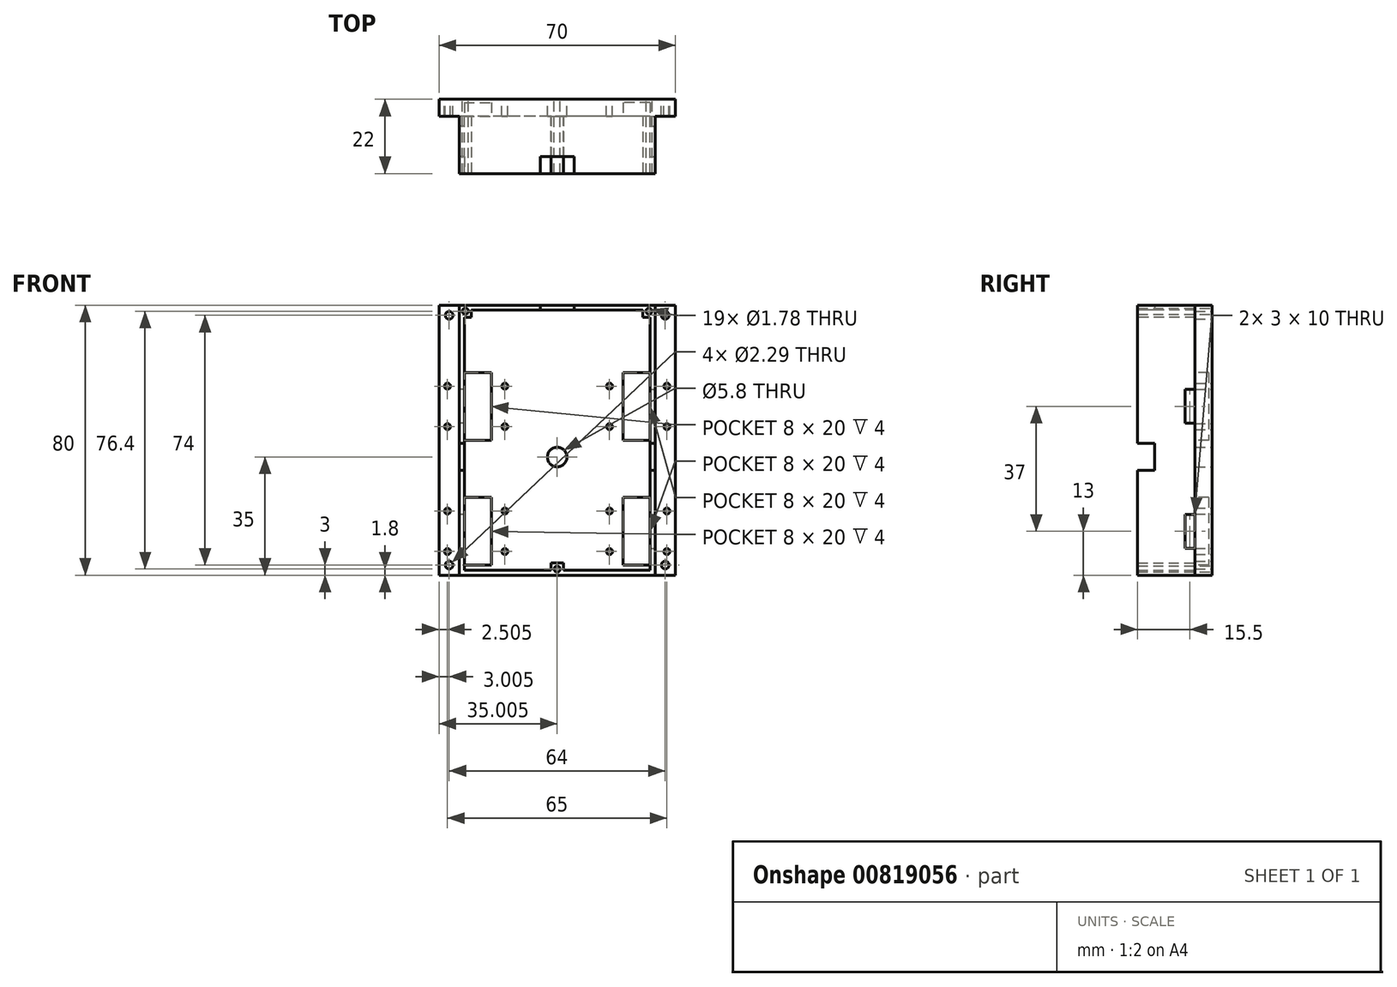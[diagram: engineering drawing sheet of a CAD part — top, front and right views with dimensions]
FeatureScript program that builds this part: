
annotation { "Feature Type Name" : "Feature", "Feature Type Description" : "" }
export const myFeature = defineFeature(function(context is Context, id is Id, definition is map)
    precondition{}
    {
        {
            var Q0;
            Q0=qCreatedBy(makeId("Front.planeOp"),FACE);
            var sketch = newSketch(context, id + "F0", { "sketchPlane" : qUnion([Q0])});
            skCircle(sketch, "E0", {"center": v(-20.58, 45.7) * mm, "radius": 0.89 * mm});
            skCircle(sketch, "E1", {"center": v(-25.88, 23.5) * mm, "radius": 0.89 * mm});
            skCircle(sketch, "E2", {"center": v(-8.88, 23.5) * mm, "radius": 0.89 * mm});
            skCircle(sketch, "E3", {"center": v(-8.88, 11.5) * mm, "radius": 0.89 * mm});
            skCircle(sketch, "E4", {"center": v(-25.88, 11.5) * mm, "radius": 0.89 * mm});
            skCircle(sketch, "E5", {"center": v(-25.88, -13.5) * mm, "radius": 0.89 * mm});
            skCircle(sketch, "E6", {"center": v(-8.88, -13.5) * mm, "radius": 0.89 * mm});
            skCircle(sketch, "E7", {"center": v(-8.88, -25.5) * mm, "radius": 0.89 * mm});
            skCircle(sketch, "E8", {"center": v(-25.88, -25.5) * mm, "radius": 0.89 * mm});
            skCircle(sketch, "E9", {"center": v(-25.38, -29.5) * mm, "radius": 1.14 * mm});
            skCircle(sketch, "E10", {"center": v(6.62, -30.7) * mm, "radius": 0.89 * mm});
            skCircle(sketch, "E11", {"center": v(6.62, 2.5) * mm, "radius": 2.9 * mm});
            skLineSegment(sketch, "E12", {"start": v(41.63, 47.5) * mm, "end": v(-28.38, 47.5) * mm});
            skLineSegment(sketch, "E13", {"start": v(-28.37, 47.5) * mm, "end": v(-28.38, -32.5) * mm});
            skLineSegment(sketch, "E14", {"start": v(41.63, -32.5) * mm, "end": v(-28.38, -32.5) * mm});
            skLineSegment(sketch, "E15.bottom", {"start": v(-28.38, -32.5) * mm, "end": v(-22.38, -32.5) * mm, "construction": true});
            skLineSegment(sketch, "E15.top", {"start": v(-28.38, -26.5) * mm, "end": v(-22.38, -26.5) * mm, "construction": true});
            skLineSegment(sketch, "E15.left", {"start": v(-28.38, -32.5) * mm, "end": v(-28.38, -26.5) * mm, "construction": true});
            skLineSegment(sketch, "E15.right", {"start": v(-22.38, -32.5) * mm, "end": v(-22.38, -26.5) * mm, "construction": true});
            skLineSegment(sketch, "E16", {"start": v(-28.37, -26.5) * mm, "end": v(-22.38, -32.5) * mm});
            skLineSegment(sketch, "E17", {"start": v(-28.38, -32.5) * mm, "end": v(-22.38, -26.5) * mm});
            skPoint(sketch, "E18", {"position": v(-28.38, 7.5) * mm});
            skLineSegment(sketch, "E19", {"start": v(6.62, 47.5) * mm, "end": v(-20.58, 47.5) * mm, "construction": true});
            skLineSegment(sketch, "E20", {"start": v(-20.58, 47.5) * mm, "end": v(-20.58, 45.7) * mm});
            skLineSegment(sketch, "E21", {"start": v(6.63, -32.5) * mm, "end": v(6.63, -30.7) * mm});
            skLineSegment(sketch, "E22", {"start": v(-8.88, -13.5) * mm, "end": v(-8.88, -25.5) * mm, "construction": true});
            skPoint(sketch, "E23", {"position": v(-8.88, -19.5) * mm});
            skLineSegment(sketch, "E24", {"start": v(-8.88, -19.5) * mm, "end": v(-28.38, -19.5) * mm, "construction": true});
            skLineSegment(sketch, "E25", {"start": v(-25.88, -25.5) * mm, "end": v(-25.88, -13.5) * mm, "construction": true});
            skPoint(sketch, "E26", {"position": v(-25.88, -19.5) * mm});
            skPoint(sketch, "E27", {"position": v(-20.88, -19.5) * mm});
            skLineSegment(sketch, "E28", {"start": v(-20.88, -19.5) * mm, "end": v(-20.88, -9.5) * mm, "construction": true});
            skLineSegment(sketch, "E29", {"start": v(-20.88, -9.5) * mm, "end": v(-12.88, -9.5) * mm, "construction": true});
            skLineSegment(sketch, "E30", {"start": v(-12.88, -9.5) * mm, "end": v(-12.88, -29.5) * mm, "construction": true});
            skLineSegment(sketch, "E31.bottom", {"start": v(-20.88, -9.5) * mm, "end": v(-12.88, -9.5) * mm});
            skLineSegment(sketch, "E31.top", {"start": v(-20.88, -29.5) * mm, "end": v(-12.88, -29.5) * mm});
            skLineSegment(sketch, "E31.left", {"start": v(-20.88, -9.5) * mm, "end": v(-20.88, -29.5) * mm});
            skLineSegment(sketch, "E31.right", {"start": v(-12.88, -9.5) * mm, "end": v(-12.88, -29.5) * mm});
            skLineSegment(sketch, "E32", {"start": v(-25.88, 23.5) * mm, "end": v(-25.88, 11.5) * mm, "construction": true});
            skPoint(sketch, "E33", {"position": v(-25.88, 17.5) * mm});
            skLineSegment(sketch, "E34", {"start": v(-8.88, 23.5) * mm, "end": v(-8.88, 11.5) * mm, "construction": true});
            skPoint(sketch, "E35", {"position": v(-8.88, 17.5) * mm});
            skLineSegment(sketch, "E36", {"start": v(-8.88, 17.5) * mm, "end": v(-28.38, 17.5) * mm, "construction": true});
            skLineSegment(sketch, "E37", {"start": v(-25.88, 23.5) * mm, "end": v(-28.38, 23.5) * mm, "construction": true});
            skLineSegment(sketch, "E38", {"start": v(-25.88, -13.5) * mm, "end": v(-28.38, -13.5) * mm, "construction": true});
            skLineSegment(sketch, "E39", {"start": v(-20.88, -9.5) * mm, "end": v(-28.38, -9.5) * mm, "construction": true});
            skLineSegment(sketch, "E40", {"start": v(-28.38, 27.5) * mm, "end": v(-20.88, 27.5) * mm, "construction": true});
            skLineSegment(sketch, "E41", {"start": v(-20.88, 27.5) * mm, "end": v(-20.88, 17.5) * mm});
            skLineSegment(sketch, "E42", {"start": v(-20.88, 27.5) * mm, "end": v(-12.88, 27.5) * mm});
            skLineSegment(sketch, "E43", {"start": v(-12.88, 27.5) * mm, "end": v(-12.87, 7.5) * mm, "construction": true});
            skLineSegment(sketch, "E44.bottom", {"start": v(-20.88, 27.5) * mm, "end": v(-12.88, 27.5) * mm, "construction": true});
            skLineSegment(sketch, "E44.top", {"start": v(-20.88, 7.5) * mm, "end": v(-12.88, 7.5) * mm});
            skLineSegment(sketch, "E44.left", {"start": v(-20.88, 27.5) * mm, "end": v(-20.88, 7.5) * mm});
            skLineSegment(sketch, "E44.right", {"start": v(-12.87, 27.5) * mm, "end": v(-12.87, 7.5) * mm});
            skLineSegment(sketch, "E45", {"start": v(41.62, 47.5) * mm, "end": v(41.63, -32.5) * mm});
            skLineSegment(sketch, "E46", {"start": v(6.62, 2.5) * mm, "end": v(6.62, -30.7) * mm});
            skLineSegment(sketch, "E47", {"start": v(6.62, 47.5) * mm, "end": v(6.62, 2.5) * mm, "construction": true});
            skLineSegment(sketch, "E48.bottom", {"start": v(-28.38, 47.5) * mm, "end": v(-22.38, 47.5) * mm, "construction": true});
            skLineSegment(sketch, "E48.top", {"start": v(-28.38, 41.5) * mm, "end": v(-22.38, 41.5) * mm, "construction": true});
            skLineSegment(sketch, "E48.left", {"start": v(-28.38, 47.5) * mm, "end": v(-28.38, 41.5) * mm, "construction": true});
            skLineSegment(sketch, "E48.right", {"start": v(-22.38, 47.5) * mm, "end": v(-22.38, 41.5) * mm, "construction": true});
            skLineSegment(sketch, "E49", {"start": v(-28.38, 47.5) * mm, "end": v(-22.38, 41.5) * mm, "construction": true});
            skLineSegment(sketch, "E50", {"start": v(-28.38, 41.5) * mm, "end": v(-22.38, 47.5) * mm, "construction": true});
            skCircle(sketch, "E51", {"center": v(-25.38, 44.5) * mm, "radius": 1.14 * mm});
            skCircle(sketch, "E52.MirrorC", {"center": v(38.62, -29.5) * mm, "radius": 1.14 * mm});
            skCircle(sketch, "E53.MirrorC", {"center": v(39.12, -25.5) * mm, "radius": 0.89 * mm});
            skLineSegment(sketch, "E54.MirrorCS", {"start": v(26.13, -9.5) * mm, "end": v(26.13, -29.5) * mm});
            skLineSegment(sketch, "E55.MirrorCS", {"start": v(34.12, -9.5) * mm, "end": v(26.13, -9.5) * mm});
            skLineSegment(sketch, "E56.MirrorCS", {"start": v(34.12, -9.5) * mm, "end": v(34.12, -29.5) * mm});
            skPoint(sketch, "E57.MirrorP", {"position": v(34.12, -19.5) * mm});
            skLineSegment(sketch, "E58.MirrorCS", {"start": v(34.12, -9.5) * mm, "end": v(26.13, -9.5) * mm, "construction": true});
            skLineSegment(sketch, "E59.MirrorCS", {"start": v(22.13, -13.5) * mm, "end": v(22.13, -25.5) * mm, "construction": true});
            skLineSegment(sketch, "E60.MirrorCS", {"start": v(34.12, -29.5) * mm, "end": v(26.13, -29.5) * mm});
            skLineSegment(sketch, "E61.MirrorCS", {"start": v(34.12, -19.5) * mm, "end": v(34.12, -9.5) * mm, "construction": true});
            skCircle(sketch, "E62.MirrorC", {"center": v(22.13, -25.5) * mm, "radius": 0.89 * mm});
            skCircle(sketch, "E63.MirrorC", {"center": v(22.13, -13.5) * mm, "radius": 0.89 * mm});
            skPoint(sketch, "E64.MirrorP", {"position": v(39.12, -19.5) * mm});
            skPoint(sketch, "E65.MirrorP", {"position": v(22.13, -19.5) * mm});
            skCircle(sketch, "E66.MirrorC", {"center": v(39.12, -13.5) * mm, "radius": 0.89 * mm});
            skLineSegment(sketch, "E67.MirrorCS", {"start": v(39.12, -25.5) * mm, "end": v(39.12, -13.5) * mm, "construction": true});
            skLineSegment(sketch, "E68.MirrorCS", {"start": v(26.13, -9.5) * mm, "end": v(26.13, -29.5) * mm, "construction": true});
            skPoint(sketch, "E69.MirrorP", {"position": v(41.63, 7.5) * mm});
            skLineSegment(sketch, "E70.MirrorCS", {"start": v(26.12, 27.5) * mm, "end": v(26.12, 7.5) * mm});
            skLineSegment(sketch, "E71.MirrorCS", {"start": v(34.12, 27.5) * mm, "end": v(26.13, 27.5) * mm});
            skCircle(sketch, "E72.MirrorC", {"center": v(39.13, 23.5) * mm, "radius": 0.89 * mm});
            skLineSegment(sketch, "E73.MirrorCS", {"start": v(34.12, 27.5) * mm, "end": v(26.13, 27.5) * mm, "construction": true});
            skLineSegment(sketch, "E74.MirrorCS", {"start": v(34.12, 7.5) * mm, "end": v(26.12, 7.5) * mm});
            skPoint(sketch, "E75.MirrorP", {"position": v(39.13, 17.5) * mm});
            skLineSegment(sketch, "E76.MirrorCS", {"start": v(34.12, 27.5) * mm, "end": v(34.12, 7.5) * mm});
            skCircle(sketch, "E77.MirrorC", {"center": v(22.13, 23.5) * mm, "radius": 0.89 * mm});
            skLineSegment(sketch, "E78.MirrorCS", {"start": v(22.13, 23.5) * mm, "end": v(22.13, 11.5) * mm, "construction": true});
            skLineSegment(sketch, "E79.MirrorCS", {"start": v(26.12, 27.5) * mm, "end": v(26.12, 7.5) * mm, "construction": true});
            skLineSegment(sketch, "E80.MirrorCS", {"start": v(39.12, 23.5) * mm, "end": v(39.12, 11.5) * mm, "construction": true});
            skLineSegment(sketch, "E81.MirrorCS", {"start": v(34.12, 27.5) * mm, "end": v(34.12, 17.5) * mm});
            skCircle(sketch, "E82.MirrorC", {"center": v(39.13, 11.5) * mm, "radius": 0.89 * mm});
            skCircle(sketch, "E83.MirrorC", {"center": v(22.13, 11.5) * mm, "radius": 0.89 * mm});
            skPoint(sketch, "E84.MirrorP", {"position": v(22.13, 17.5) * mm});
            skCircle(sketch, "E85.MirrorC", {"center": v(38.63, 44.5) * mm, "radius": 1.14 * mm});
            skCircle(sketch, "E86.MirrorC", {"center": v(33.83, 45.7) * mm, "radius": 0.89 * mm});
            skLineSegment(sketch, "E87", {"start": v(34.12, -29.5) * mm, "end": v(35.62, -29.5) * mm, "construction": true});
            skLineSegment(sketch, "E88", {"start": v(35.62, -29.5) * mm, "end": v(35.62, -32.5) * mm});
            skLineSegment(sketch, "E89", {"start": v(35.62, -29.5) * mm, "end": v(35.62, 47.5) * mm});
            skLineSegment(sketch, "E90", {"start": v(-20.88, -29.5) * mm, "end": v(-22.38, -29.5) * mm, "construction": true});
            skLineSegment(sketch, "E91.bottom", {"start": v(-22.38, 47.5) * mm, "end": v(35.62, 47.5) * mm});
            skLineSegment(sketch, "E91.top", {"start": v(-22.38, -32.5) * mm, "end": v(35.62, -32.5) * mm});
            skLineSegment(sketch, "E91.left", {"start": v(-22.38, 47.5) * mm, "end": v(-22.38, -32.5) * mm});
            skLineSegment(sketch, "E91.right", {"start": v(35.62, 47.5) * mm, "end": v(35.62, -32.5) * mm});
            skLineSegment(sketch, "E92", {"start": v(-20.58, 45.7) * mm, "end": v(-18.78, 45.7) * mm, "construction": true});
            skLineSegment(sketch, "E93", {"start": v(-18.78, 45.7) * mm, "end": v(-18.78, 43.9) * mm, "construction": true});
            skLineSegment(sketch, "E94.bottom", {"start": v(-18.78, 43.9) * mm, "end": v(-22.38, 43.9) * mm});
            skLineSegment(sketch, "E94.top", {"start": v(-18.78, 47.5) * mm, "end": v(-22.38, 47.5) * mm});
            skLineSegment(sketch, "E94.left", {"start": v(-18.78, 43.9) * mm, "end": v(-18.78, 47.5) * mm});
            skLineSegment(sketch, "E94.right", {"start": v(-22.38, 43.9) * mm, "end": v(-22.38, 47.5) * mm});
            skLineSegment(sketch, "E95", {"start": v(33.83, 45.7) * mm, "end": v(32.03, 45.7) * mm, "construction": true});
            skLineSegment(sketch, "E96", {"start": v(32.03, 45.7) * mm, "end": v(32.03, 43.9) * mm, "construction": true});
            skLineSegment(sketch, "E97.bottom", {"start": v(32.03, 43.9) * mm, "end": v(35.62, 43.9) * mm});
            skLineSegment(sketch, "E97.top", {"start": v(32.03, 47.5) * mm, "end": v(35.62, 47.5) * mm});
            skLineSegment(sketch, "E97.left", {"start": v(32.03, 43.9) * mm, "end": v(32.03, 47.5) * mm});
            skLineSegment(sketch, "E97.right", {"start": v(35.62, 43.9) * mm, "end": v(35.62, 47.5) * mm});
            skLineSegment(sketch, "E98", {"start": v(6.62, -30.7) * mm, "end": v(4.82, -30.7) * mm});
            skLineSegment(sketch, "E99", {"start": v(4.82, -30.7) * mm, "end": v(4.82, -28.9) * mm});
            skLineSegment(sketch, "E100", {"start": v(6.63, -32.5) * mm, "end": v(8.43, -32.5) * mm});
            skLineSegment(sketch, "E101.bottom", {"start": v(8.43, -32.5) * mm, "end": v(4.82, -32.5) * mm});
            skLineSegment(sketch, "E101.top", {"start": v(8.43, -28.9) * mm, "end": v(4.82, -28.9) * mm});
            skLineSegment(sketch, "E101.left", {"start": v(8.43, -32.5) * mm, "end": v(8.43, -28.9) * mm});
            skLineSegment(sketch, "E101.right", {"start": v(4.82, -32.5) * mm, "end": v(4.82, -28.9) * mm});
            skLineSegment(sketch, "E102", {"start": v(34.13, 17.5) * mm, "end": v(37.13, 17.5) * mm, "construction": true});
            skLineSegment(sketch, "E103.bottom", {"start": v(33.13, 22.5) * mm, "end": v(37.13, 22.5) * mm});
            skLineSegment(sketch, "E103.top", {"start": v(33.13, 12.5) * mm, "end": v(37.13, 12.5) * mm});
            skLineSegment(sketch, "E103.left", {"start": v(33.12, 22.5) * mm, "end": v(33.12, 12.5) * mm});
            skLineSegment(sketch, "E103.right", {"start": v(37.13, 22.5) * mm, "end": v(37.13, 12.5) * mm});
            skPoint(sketch, "E104", {"position": v(37.13, 17.5) * mm});
            skLineSegment(sketch, "E105.MirrorCS", {"start": v(-19.88, 12.5) * mm, "end": v(-23.88, 12.5) * mm});
            skLineSegment(sketch, "E106.MirrorCS", {"start": v(-23.87, 22.5) * mm, "end": v(-23.87, 12.5) * mm});
            skLineSegment(sketch, "E107.MirrorCS", {"start": v(-19.87, 22.5) * mm, "end": v(-19.87, 12.5) * mm});
            skLineSegment(sketch, "E108.MirrorCS", {"start": v(-19.88, 22.5) * mm, "end": v(-23.88, 22.5) * mm});
            skLineSegment(sketch, "E109", {"start": v(34.12, -19.5) * mm, "end": v(37.13, -19.5) * mm, "construction": true});
            skLineSegment(sketch, "E110.bottom", {"start": v(33.12, -14.5) * mm, "end": v(37.13, -14.5) * mm});
            skLineSegment(sketch, "E110.top", {"start": v(33.12, -24.5) * mm, "end": v(37.13, -24.5) * mm});
            skLineSegment(sketch, "E110.left", {"start": v(33.12, -14.5) * mm, "end": v(33.12, -24.5) * mm});
            skLineSegment(sketch, "E110.right", {"start": v(37.13, -14.5) * mm, "end": v(37.13, -24.5) * mm});
            skPoint(sketch, "E111", {"position": v(37.13, -19.5) * mm});
            skLineSegment(sketch, "E112.MirrorCS", {"start": v(-19.88, -24.5) * mm, "end": v(-23.88, -24.5) * mm});
            skLineSegment(sketch, "E113.MirrorCS", {"start": v(-19.87, -14.5) * mm, "end": v(-19.87, -24.5) * mm});
            skLineSegment(sketch, "E114.MirrorCS", {"start": v(-23.87, -14.5) * mm, "end": v(-23.87, -24.5) * mm});
            skLineSegment(sketch, "E115.MirrorCS", {"start": v(-19.88, -14.5) * mm, "end": v(-23.88, -14.5) * mm});
            skLineSegment(sketch, "E116.bottom", {"start": v(31.62, 6.5) * mm, "end": v(35.62, 6.5) * mm});
            skLineSegment(sketch, "E116.top", {"start": v(31.62, -1.5) * mm, "end": v(35.62, -1.5) * mm});
            skLineSegment(sketch, "E116.left", {"start": v(31.62, 6.5) * mm, "end": v(31.62, -1.5) * mm});
            skLineSegment(sketch, "E116.right", {"start": v(35.62, 6.5) * mm, "end": v(35.62, -1.5) * mm});
            skPoint(sketch, "E117", {"position": v(35.62, 2.5) * mm});
            skLineSegment(sketch, "E118.MirrorCS", {"start": v(-18.38, -1.5) * mm, "end": v(-22.38, -1.5) * mm});
            skLineSegment(sketch, "E119.MirrorCS", {"start": v(-22.38, 6.5) * mm, "end": v(-22.38, -1.5) * mm});
            skLineSegment(sketch, "E120.MirrorCS", {"start": v(-18.38, 6.5) * mm, "end": v(-22.38, 6.5) * mm});
            skLineSegment(sketch, "E121.MirrorCS", {"start": v(-18.38, 6.5) * mm, "end": v(-18.38, -1.5) * mm});
            skLineSegment(sketch, "E122.bottom", {"start": v(1.63, 47.5) * mm, "end": v(11.62, 47.5) * mm});
            skLineSegment(sketch, "E122.top", {"start": v(1.63, 43.5) * mm, "end": v(11.62, 43.5) * mm});
            skLineSegment(sketch, "E122.left", {"start": v(1.62, 47.5) * mm, "end": v(1.63, 43.5) * mm});
            skLineSegment(sketch, "E122.right", {"start": v(11.62, 47.5) * mm, "end": v(11.62, 43.5) * mm});
            skPoint(sketch, "E123", {"position": v(6.62, 47.5) * mm});
            skLineSegment(sketch, "E124", {"start": v(-22.38, 47.5) * mm, "end": v(-20.58, 47.5) * mm});
            skLineSegment(sketch, "E125", {"start": v(6.62, 2.5) * mm, "end": v(35.62, 2.5) * mm, "construction": true});
            skSolve(sketch);
        }
        {
            var Q0;
            Q0=qCreatedBy(makeId("Front.planeOp"),FACE);
            var sketch = newSketch(context, id + "F1", { "sketchPlane" : qUnion([Q0])});
            skLineSegment(sketch, "E126.0", {"start": v(41.63, 47.5) * mm, "end": v(-28.38, 47.5) * mm});
            skLineSegment(sketch, "E126.1", {"start": v(-28.37, 47.5) * mm, "end": v(-28.38, -32.5) * mm});
            skLineSegment(sketch, "E126.2", {"start": v(41.62, 47.5) * mm, "end": v(41.63, -32.5) * mm});
            skLineSegment(sketch, "E126.3", {"start": v(41.63, -32.5) * mm, "end": v(-28.38, -32.5) * mm});
            skSolve(sketch);
        }
        {
            var Q0;
            Q0=qCreatedBy(makeId("Front.planeOp"),FACE);
            var sketch = newSketch(context, id + "F2", { "sketchPlane" : qUnion([Q0])});
            skLineSegment(sketch, "E127.0", {"start": v(-20.88, 7.5) * mm, "end": v(-12.88, 7.5) * mm});
            skLineSegment(sketch, "E127.1", {"start": v(-12.87, 27.5) * mm, "end": v(-12.87, 7.5) * mm});
            skLineSegment(sketch, "E127.2", {"start": v(-20.88, 27.5) * mm, "end": v(-12.88, 27.5) * mm});
            skLineSegment(sketch, "E127.3", {"start": v(-20.88, 27.5) * mm, "end": v(-20.88, 17.5) * mm});
            skLineSegment(sketch, "E127.4", {"start": v(-20.88, -9.5) * mm, "end": v(-12.88, -9.5) * mm});
            skLineSegment(sketch, "E127.5", {"start": v(-20.88, -9.5) * mm, "end": v(-20.88, -29.5) * mm});
            skLineSegment(sketch, "E127.6", {"start": v(-12.88, -9.5) * mm, "end": v(-12.88, -29.5) * mm});
            skLineSegment(sketch, "E127.7", {"start": v(-20.88, -29.5) * mm, "end": v(-12.88, -29.5) * mm});
            skLineSegment(sketch, "E127.17", {"start": v(-20.88, 27.5) * mm, "end": v(-20.88, 7.5) * mm});
            skLineSegment(sketch, "E128.0", {"start": v(34.12, 27.5) * mm, "end": v(26.13, 27.5) * mm});
            skLineSegment(sketch, "E128.1", {"start": v(26.12, 27.5) * mm, "end": v(26.12, 7.5) * mm});
            skLineSegment(sketch, "E128.2", {"start": v(34.12, 27.5) * mm, "end": v(34.12, 17.5) * mm});
            skLineSegment(sketch, "E128.3", {"start": v(34.12, 27.5) * mm, "end": v(34.12, 7.5) * mm});
            skLineSegment(sketch, "E128.4", {"start": v(34.12, 7.5) * mm, "end": v(26.12, 7.5) * mm});
            skLineSegment(sketch, "E128.5", {"start": v(34.12, -9.5) * mm, "end": v(34.12, -29.5) * mm});
            skLineSegment(sketch, "E128.6", {"start": v(34.12, -9.5) * mm, "end": v(26.13, -9.5) * mm});
            skLineSegment(sketch, "E128.7", {"start": v(26.13, -9.5) * mm, "end": v(26.13, -29.5) * mm});
            skLineSegment(sketch, "E128.8", {"start": v(34.12, -29.5) * mm, "end": v(26.13, -29.5) * mm});
            skSolve(sketch);
        }
        {
            var Q0;
            Q0=qCreatedBy(makeId("Front.planeOp"),FACE);
            var sketch = newSketch(context, id + "F3", { "sketchPlane" : qUnion([Q0])});
            skCircle(sketch, "E129.0", {"center": v(-25.88, 23.5) * mm, "radius": 0.89 * mm});
            skCircle(sketch, "E129.1", {"center": v(-25.88, 11.5) * mm, "radius": 0.89 * mm});
            skCircle(sketch, "E129.2", {"center": v(-8.88, 23.5) * mm, "radius": 0.89 * mm});
            skCircle(sketch, "E129.3", {"center": v(-8.88, 11.5) * mm, "radius": 0.89 * mm});
            skCircle(sketch, "E129.10", {"center": v(-8.88, -13.5) * mm, "radius": 0.89 * mm});
            skCircle(sketch, "E129.11", {"center": v(-25.88, -13.5) * mm, "radius": 0.89 * mm});
            skCircle(sketch, "E129.12", {"center": v(-25.88, -25.5) * mm, "radius": 0.89 * mm});
            skCircle(sketch, "E129.13", {"center": v(-8.88, -25.5) * mm, "radius": 0.89 * mm});
            skCircle(sketch, "E129.21", {"center": v(6.62, -30.7) * mm, "radius": 0.89 * mm});
            skCircle(sketch, "E129.22", {"center": v(-25.38, -29.5) * mm, "radius": 1.14 * mm});
            skCircle(sketch, "E130.0", {"center": v(6.62, 2.5) * mm, "radius": 2.9 * mm});
            skCircle(sketch, "E131.0", {"center": v(-25.38, 44.5) * mm, "radius": 1.14 * mm});
            skCircle(sketch, "E131.1", {"center": v(22.13, 23.5) * mm, "radius": 0.89 * mm});
            skCircle(sketch, "E131.2", {"center": v(22.13, 11.5) * mm, "radius": 0.89 * mm});
            skCircle(sketch, "E131.3", {"center": v(39.13, 23.5) * mm, "radius": 0.89 * mm});
            skCircle(sketch, "E131.4", {"center": v(38.63, 44.5) * mm, "radius": 1.14 * mm});
            skCircle(sketch, "E131.5", {"center": v(22.13, -13.5) * mm, "radius": 0.89 * mm});
            skCircle(sketch, "E131.6", {"center": v(22.13, -25.5) * mm, "radius": 0.89 * mm});
            skCircle(sketch, "E131.7", {"center": v(39.12, -13.5) * mm, "radius": 0.89 * mm});
            skCircle(sketch, "E131.8", {"center": v(39.12, -25.5) * mm, "radius": 0.89 * mm});
            skCircle(sketch, "E131.9", {"center": v(38.62, -29.5) * mm, "radius": 1.14 * mm});
            skCircle(sketch, "E131.10", {"center": v(39.13, 11.5) * mm, "radius": 0.89 * mm});
            skCircle(sketch, "E132.0", {"center": v(-20.58, 45.7) * mm, "radius": 0.89 * mm});
            skCircle(sketch, "E132.1", {"center": v(33.83, 45.7) * mm, "radius": 0.89 * mm});
            skSolve(sketch);
        }
        {
            var Q0;
            Q0=qSketchRegion(id+"F1",true);
            extrude(context, id + "F4", {"entities" : qUnion([Q0]), "depth" : 5 * mm, "offsetDistance" : 25 * mm});
        }
        {
            var Q0;
            Q0=qCreatedBy(makeId("Front.planeOp"),FACE);
            var sketch = newSketch(context, id + "F5", { "sketchPlane" : qUnion([Q0])});
            skLineSegment(sketch, "E133.0", {"start": v(-22.38, 47.5) * mm, "end": v(-22.38, -32.5) * mm});
            skLineSegment(sketch, "E133.1", {"start": v(-22.38, 47.5) * mm, "end": v(35.62, 47.5) * mm});
            skLineSegment(sketch, "E133.2", {"start": v(35.62, -29.5) * mm, "end": v(35.62, 47.5) * mm});
            skLineSegment(sketch, "E133.4", {"start": v(35.62, 47.5) * mm, "end": v(35.62, -32.5) * mm});
            skLineSegment(sketch, "E134.0", {"start": v(-22.38, -32.5) * mm, "end": v(35.62, -32.5) * mm});
            skLineSegment(sketch, "E135.0", {"start": v(-20.88, 46) * mm, "end": v(34.12, 46) * mm});
            skLineSegment(sketch, "E135.1", {"start": v(-20.88, 46) * mm, "end": v(-20.88, -31) * mm});
            skLineSegment(sketch, "E135.2", {"start": v(-20.88, -31) * mm, "end": v(34.12, -31) * mm});
            skLineSegment(sketch, "E135.3", {"start": v(34.12, 46) * mm, "end": v(34.12, -31) * mm});
            skSolve(sketch);
        }
        {
            var Q0;
            Q0=qCreatedBy(makeId("Front.planeOp"),FACE);
            var sketch = newSketch(context, id + "F6", { "sketchPlane" : qUnion([Q0])});
            skLineSegment(sketch, "E136.0", {"start": v(-18.78, 43.9) * mm, "end": v(-18.78, 47.5) * mm});
            skLineSegment(sketch, "E136.1", {"start": v(-18.78, 43.9) * mm, "end": v(-22.38, 43.9) * mm});
            skLineSegment(sketch, "E136.2", {"start": v(-18.78, 47.5) * mm, "end": v(-22.38, 47.5) * mm});
            skLineSegment(sketch, "E136.3", {"start": v(-22.38, 43.9) * mm, "end": v(-22.38, 47.5) * mm});
            skLineSegment(sketch, "E137.0", {"start": v(32.03, 43.9) * mm, "end": v(35.62, 43.9) * mm});
            skLineSegment(sketch, "E137.1", {"start": v(32.03, 43.9) * mm, "end": v(32.03, 47.5) * mm});
            skLineSegment(sketch, "E137.2", {"start": v(35.62, 43.9) * mm, "end": v(35.62, 47.5) * mm});
            skLineSegment(sketch, "E137.3", {"start": v(32.03, 47.5) * mm, "end": v(35.62, 47.5) * mm});
            skLineSegment(sketch, "E138.0", {"start": v(8.43, -28.9) * mm, "end": v(4.82, -28.9) * mm});
            skLineSegment(sketch, "E138.1", {"start": v(8.43, -32.5) * mm, "end": v(8.43, -28.9) * mm});
            skLineSegment(sketch, "E138.2", {"start": v(4.82, -30.7) * mm, "end": v(4.82, -28.9) * mm});
            skLineSegment(sketch, "E138.3", {"start": v(4.82, -32.5) * mm, "end": v(4.82, -28.9) * mm});
            skLineSegment(sketch, "E138.4", {"start": v(8.43, -32.5) * mm, "end": v(4.82, -32.5) * mm});
            skSolve(sketch);
        }
        {
            var Q0;
            Q0 = qSketchRegion(id + "F5", true);
            extrude(context, id + "F7", {"entities" : qUnion([Q0]), "operationType" : NewBodyOperationType.ADD, "depth" : 22 * mm, "offsetDistance" : 25 * mm});
        }
        {
            var Q0;
            Q0 = qSketchRegion(id + "F6", true);
            extrude(context, id + "F8", {"entities" : qUnion([Q0]), "operationType" : NewBodyOperationType.ADD, "depth" : 22 * mm, "offsetDistance" : 25 * mm});
        }
        {
            var Q0;
            Q0 = qSketchRegion(id + "F3", true);
            extrude(context, id + "F9", {"entities" : qUnion([Q0]), "operationType" : NewBodyOperationType.REMOVE, "endBound" : BoundingType.THROUGH_ALL, "depth" : 25 * mm, "offsetDistance" : 25 * mm});
        }
        {
            var Q0;
            {var subQ0=sQuery(id+"F1.wireOp",EDGE,"E126.1");var subQ1=sQuery(id+"F1.wireOp",EDGE,"E126.3");var subQ2=sQuery(id+"F1.wireOp",EDGE,"E126.0");Q0=makeQuery(id+"F7.boolean.opBoolean","SPLIT",FACE,{"disambiguationData":[TD([makeQuery(id+"F4.opExtrude","SWEPT_FACE",FACE,{"disambiguationData":[OSD([subQ0])]})])],"derivedFrom":makeQuery(id+"F4.opExtrude","CAP_FACE",FACE,{"disambiguationData":[OSD([subQ2,subQ0,sQuery(id+"F1.wireOp",EDGE,"E126.2"),subQ1])],"isStart":false})});}
            var sketch = newSketch(context, id + "F10", { "sketchPlane" : qUnion([Q0])});
            skLineSegment(sketch, "E139.0", {"start": v(-19.87, 22.5) * mm, "end": v(-23.87, 22.5) * mm});
            skLineSegment(sketch, "E139.1", {"start": v(-23.87, 22.5) * mm, "end": v(-23.87, 12.5) * mm});
            skLineSegment(sketch, "E139.2", {"start": v(-19.87, 22.5) * mm, "end": v(-19.87, 12.5) * mm});
            skLineSegment(sketch, "E139.3", {"start": v(-19.87, 12.5) * mm, "end": v(-23.87, 12.5) * mm});
            skLineSegment(sketch, "E140.0", {"start": v(-19.88, -14.5) * mm, "end": v(-23.88, -14.5) * mm});
            skLineSegment(sketch, "E140.1", {"start": v(-23.87, -14.5) * mm, "end": v(-23.87, -24.5) * mm});
            skLineSegment(sketch, "E140.2", {"start": v(-19.87, -14.5) * mm, "end": v(-19.87, -24.5) * mm});
            skLineSegment(sketch, "E140.3", {"start": v(-19.88, -24.5) * mm, "end": v(-23.88, -24.5) * mm});
            skLineSegment(sketch, "E141.0", {"start": v(33.12, -14.5) * mm, "end": v(37.13, -14.5) * mm});
            skLineSegment(sketch, "E141.1", {"start": v(33.12, -14.5) * mm, "end": v(33.12, -24.5) * mm});
            skLineSegment(sketch, "E141.2", {"start": v(37.13, -14.5) * mm, "end": v(37.13, -24.5) * mm});
            skLineSegment(sketch, "E141.3", {"start": v(33.12, -24.5) * mm, "end": v(37.13, -24.5) * mm});
            skLineSegment(sketch, "E142.0", {"start": v(33.13, 22.5) * mm, "end": v(37.13, 22.5) * mm});
            skLineSegment(sketch, "E142.1", {"start": v(33.12, 22.5) * mm, "end": v(33.12, 12.5) * mm});
            skLineSegment(sketch, "E142.2", {"start": v(33.13, 12.5) * mm, "end": v(37.13, 12.5) * mm});
            skLineSegment(sketch, "E142.3", {"start": v(37.13, 22.5) * mm, "end": v(37.13, 12.5) * mm});
            skSolve(sketch);
        }
        {
            var Q0;
            Q0 = qSketchRegion(id + "F10", true);
            extrude(context, id + "F11", {"entities" : qUnion([Q0]), "operationType" : NewBodyOperationType.REMOVE, "depth" : 3 * mm, "offsetDistance" : 25 * mm});
        }
        {
            var Q0;
            Q0=makeQuery(id+"F8.boolean.opBoolean","MERGE",FACE,{"derivedFrom":[makeQuery(id+"F7.opExtrude","CAP_FACE",FACE,{"disambiguationData":[OSD([sQuery(id+"F5.wireOp",EDGE,"E133.0"),sQuery(id+"F5.wireOp",EDGE,"E133.1"),sQuery(id+"F5.wireOp",EDGE,"E133.4"),sQuery(id+"F5.wireOp",EDGE,"E134.0"),sQuery(id+"F5.wireOp",EDGE,"E135.0"),sQuery(id+"F5.wireOp",EDGE,"E135.1"),sQuery(id+"F5.wireOp",EDGE,"E135.2"),sQuery(id+"F5.wireOp",EDGE,"E135.3")])],"isStart":false}),makeQuery(id+"F8.opExtrude","CAP_FACE",FACE,{"disambiguationData":[OSD([sQuery(id+"F6.wireOp",EDGE,"E136.0"),sQuery(id+"F6.wireOp",EDGE,"E136.1"),sQuery(id+"F6.wireOp",EDGE,"E136.2"),sQuery(id+"F6.wireOp",EDGE,"E136.3")])],"isStart":false}),makeQuery(id+"F8.opExtrude","CAP_FACE",FACE,{"disambiguationData":[OSD([sQuery(id+"F6.wireOp",EDGE,"E137.0"),sQuery(id+"F6.wireOp",EDGE,"E137.1"),sQuery(id+"F6.wireOp",EDGE,"E137.2"),sQuery(id+"F6.wireOp",EDGE,"E137.3")])],"isStart":false}),makeQuery(id+"F8.opExtrude","CAP_FACE",FACE,{"disambiguationData":[OSD([sQuery(id+"F6.wireOp",EDGE,"E138.0"),sQuery(id+"F6.wireOp",EDGE,"E138.1"),sQuery(id+"F6.wireOp",EDGE,"E138.3"),sQuery(id+"F6.wireOp",EDGE,"E138.4")])],"isStart":false})]});
            var sketch = newSketch(context, id + "F12", { "sketchPlane" : qUnion([Q0])});
            skLineSegment(sketch, "E143.0", {"start": v(1.63, 43.5) * mm, "end": v(11.62, 43.5) * mm});
            skLineSegment(sketch, "E143.1", {"start": v(1.63, 47.5) * mm, "end": v(11.62, 47.5) * mm});
            skLineSegment(sketch, "E143.2", {"start": v(11.62, 47.5) * mm, "end": v(11.62, 43.5) * mm});
            skLineSegment(sketch, "E143.3", {"start": v(1.62, 47.5) * mm, "end": v(1.63, 43.5) * mm});
            skLineSegment(sketch, "E143.4", {"start": v(31.62, 6.5) * mm, "end": v(35.62, 6.5) * mm});
            skLineSegment(sketch, "E143.5", {"start": v(31.62, 6.5) * mm, "end": v(31.62, -1.5) * mm});
            skLineSegment(sketch, "E143.6", {"start": v(31.62, -1.5) * mm, "end": v(35.62, -1.5) * mm});
            skLineSegment(sketch, "E143.7", {"start": v(35.62, 6.5) * mm, "end": v(35.62, -1.5) * mm});
            skLineSegment(sketch, "E143.8", {"start": v(-18.38, 6.5) * mm, "end": v(-22.38, 6.5) * mm});
            skLineSegment(sketch, "E143.9", {"start": v(-22.38, 6.5) * mm, "end": v(-22.38, -1.5) * mm});
            skLineSegment(sketch, "E143.10", {"start": v(-18.38, 6.5) * mm, "end": v(-18.38, -1.5) * mm});
            skLineSegment(sketch, "E143.11", {"start": v(-18.38, -1.5) * mm, "end": v(-22.38, -1.5) * mm});
            skSolve(sketch);
        }
        {
            var Q0;
            Q0 = qSketchRegion(id + "F12", true);
            extrude(context, id + "F13", {"entities" : qUnion([Q0]), "operationType" : NewBodyOperationType.REMOVE, "oppositeDirection" : true, "depth" : 5 * mm, "offsetDistance" : 25 * mm});
        }
        {
            var Q0;
            {var subQ0=sQuery(id+"F1.wireOp",EDGE,"E126.3");var subQ1=sQuery(id+"F1.wireOp",EDGE,"E126.2");var subQ2=sQuery(id+"F1.wireOp",EDGE,"E126.1");var subQ3=sQuery(id+"F1.wireOp",EDGE,"E126.0");var subQ4=makeQuery(id+"F4.opExtrude","CAP_FACE",FACE,{"disambiguationData":[OSD([subQ3,subQ2,subQ1,subQ0])],"isStart":false});Q0=makeQuery(id+"F11.boolean.opBoolean","MERGE",FACE,{"derivedFrom":[makeQuery(id+"F7.boolean.opBoolean","SPLIT",FACE,{"disambiguationData":[TD([makeQuery(id+"F4.opExtrude","SWEPT_FACE",FACE,{"disambiguationData":[OSD([subQ2])]})])],"derivedFrom":subQ4}),makeQuery(id+"F7.boolean.opBoolean","SPLIT",FACE,{"disambiguationData":[TD([makeQuery(id+"F4.opExtrude","SWEPT_FACE",FACE,{"disambiguationData":[OSD([subQ1])]})])],"derivedFrom":subQ4}),makeQuery(id+"F7.boolean.opBoolean","SPLIT",FACE,{"disambiguationData":[TD([makeQuery(id+"F7.opExtrude","SWEPT_FACE",FACE,{"disambiguationData":[OSD([sQuery(id+"F5.wireOp",EDGE,"E135.0")])]})])],"derivedFrom":subQ4})],"fromTools":[makeQuery(id+"F11.opExtrude","CAP_FACE",FACE,{"disambiguationData":[OSD([sQuery(id+"F10.wireOp",EDGE,"E139.0"),sQuery(id+"F10.wireOp",EDGE,"E139.1"),sQuery(id+"F10.wireOp",EDGE,"E139.2"),sQuery(id+"F10.wireOp",EDGE,"E139.3")])],"isStart":true}),makeQuery(id+"F11.opExtrude","CAP_FACE",FACE,{"disambiguationData":[OSD([sQuery(id+"F10.wireOp",EDGE,"E140.0"),sQuery(id+"F10.wireOp",EDGE,"E140.1"),sQuery(id+"F10.wireOp",EDGE,"E140.2"),sQuery(id+"F10.wireOp",EDGE,"E140.3")])],"isStart":true}),makeQuery(id+"F11.opExtrude","CAP_FACE",FACE,{"disambiguationData":[OSD([sQuery(id+"F10.wireOp",EDGE,"E141.0"),sQuery(id+"F10.wireOp",EDGE,"E141.1"),sQuery(id+"F10.wireOp",EDGE,"E141.2"),sQuery(id+"F10.wireOp",EDGE,"E141.3")])],"isStart":true}),makeQuery(id+"F11.opExtrude","CAP_FACE",FACE,{"disambiguationData":[OSD([sQuery(id+"F10.wireOp",EDGE,"E142.0"),sQuery(id+"F10.wireOp",EDGE,"E142.1"),sQuery(id+"F10.wireOp",EDGE,"E142.2"),sQuery(id+"F10.wireOp",EDGE,"E142.3")])],"isStart":true})]});}
            var sketch = newSketch(context, id + "F14", { "sketchPlane" : qUnion([Q0])});
            skLineSegment(sketch, "E144.0", {"start": v(-20.88, 7.5) * mm, "end": v(-12.88, 7.5) * mm});
            skLineSegment(sketch, "E144.1", {"start": v(-12.87, 27.5) * mm, "end": v(-12.87, 7.5) * mm});
            skLineSegment(sketch, "E144.2", {"start": v(-20.88, 27.5) * mm, "end": v(-12.88, 27.5) * mm});
            skLineSegment(sketch, "E144.3", {"start": v(-20.88, 27.5) * mm, "end": v(-20.88, 17.5) * mm});
            skLineSegment(sketch, "E144.4", {"start": v(-20.88, -9.5) * mm, "end": v(-12.88, -9.5) * mm});
            skLineSegment(sketch, "E144.5", {"start": v(-20.88, -9.5) * mm, "end": v(-20.88, -29.5) * mm});
            skLineSegment(sketch, "E144.6", {"start": v(-12.88, -9.5) * mm, "end": v(-12.88, -29.5) * mm});
            skLineSegment(sketch, "E144.7", {"start": v(-20.88, -29.5) * mm, "end": v(-12.88, -29.5) * mm});
            skLineSegment(sketch, "E144.8", {"start": v(-20.88, 27.5) * mm, "end": v(-20.88, 7.5) * mm});
            skLineSegment(sketch, "E144.9", {"start": v(34.12, 27.5) * mm, "end": v(26.13, 27.5) * mm});
            skLineSegment(sketch, "E144.10", {"start": v(26.12, 27.5) * mm, "end": v(26.12, 7.5) * mm});
            skLineSegment(sketch, "E144.11", {"start": v(34.12, 27.5) * mm, "end": v(34.12, 17.5) * mm});
            skLineSegment(sketch, "E144.12", {"start": v(34.12, 27.5) * mm, "end": v(34.12, 7.5) * mm});
            skLineSegment(sketch, "E144.13", {"start": v(34.12, 7.5) * mm, "end": v(26.12, 7.5) * mm});
            skLineSegment(sketch, "E144.14", {"start": v(34.12, -9.5) * mm, "end": v(34.12, -29.5) * mm});
            skLineSegment(sketch, "E144.15", {"start": v(34.12, -9.5) * mm, "end": v(26.13, -9.5) * mm});
            skLineSegment(sketch, "E144.16", {"start": v(26.13, -9.5) * mm, "end": v(26.13, -29.5) * mm});
            skLineSegment(sketch, "E144.17", {"start": v(34.12, -29.5) * mm, "end": v(26.13, -29.5) * mm});
            skLineSegment(sketch, "E144.18", {"start": v(-20.88, 27.5) * mm, "end": v(-12.88, 27.5) * mm});
            skSolve(sketch);
        }
        {
            var Q0;
            Q0 = qSketchRegion(id + "F14", true);
            extrude(context, id + "F15", {"entities" : qUnion([Q0]), "operationType" : NewBodyOperationType.REMOVE, "oppositeDirection" : true, "depth" : 4 * mm, "offsetDistance" : 25 * mm});
        }
    });
